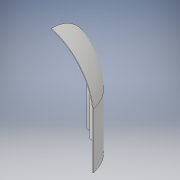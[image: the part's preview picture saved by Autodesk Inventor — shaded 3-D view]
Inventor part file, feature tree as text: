
AUTODESK INVENTOR PART (.ipt)
format: ipt  version: 2019 (Build 230136000, 136)  size: 294,912 bytes
history: native  units: mm
features: sketch x6, extrude x3, other x2, loft x1, shell x1, projected_geometry x1
ambient origin geometry x8: Origin, YZ Plane, XZ Plane, XY Plane, X Axis, Y Axis, Z Axis, Center Point
bodies: Body1 (feature_tree)
feature tree (14):
  other  "правое надкрылье"
  sketch  "Эскиз3"
  sketch  "Эскиз4"
  other  "РабПлоскость1"
  loft  "Лофт1"
  extrude  "Выдавливание2"  Depth=100.0mm
  shell  "Оболочка1"  Thickness=17.0mm
  extrude  "Выдавливание3"  Depth=4.0mm
  extrude  "Выдавливание6"  Depth=35.0mm
  sketch  "Эскиз5"
  sketch  "Эскиз6"
  projected_geometry  "Спроецированная петля1"
  sketch  "Эскиз7"
  sketch  "Эскиз10"
